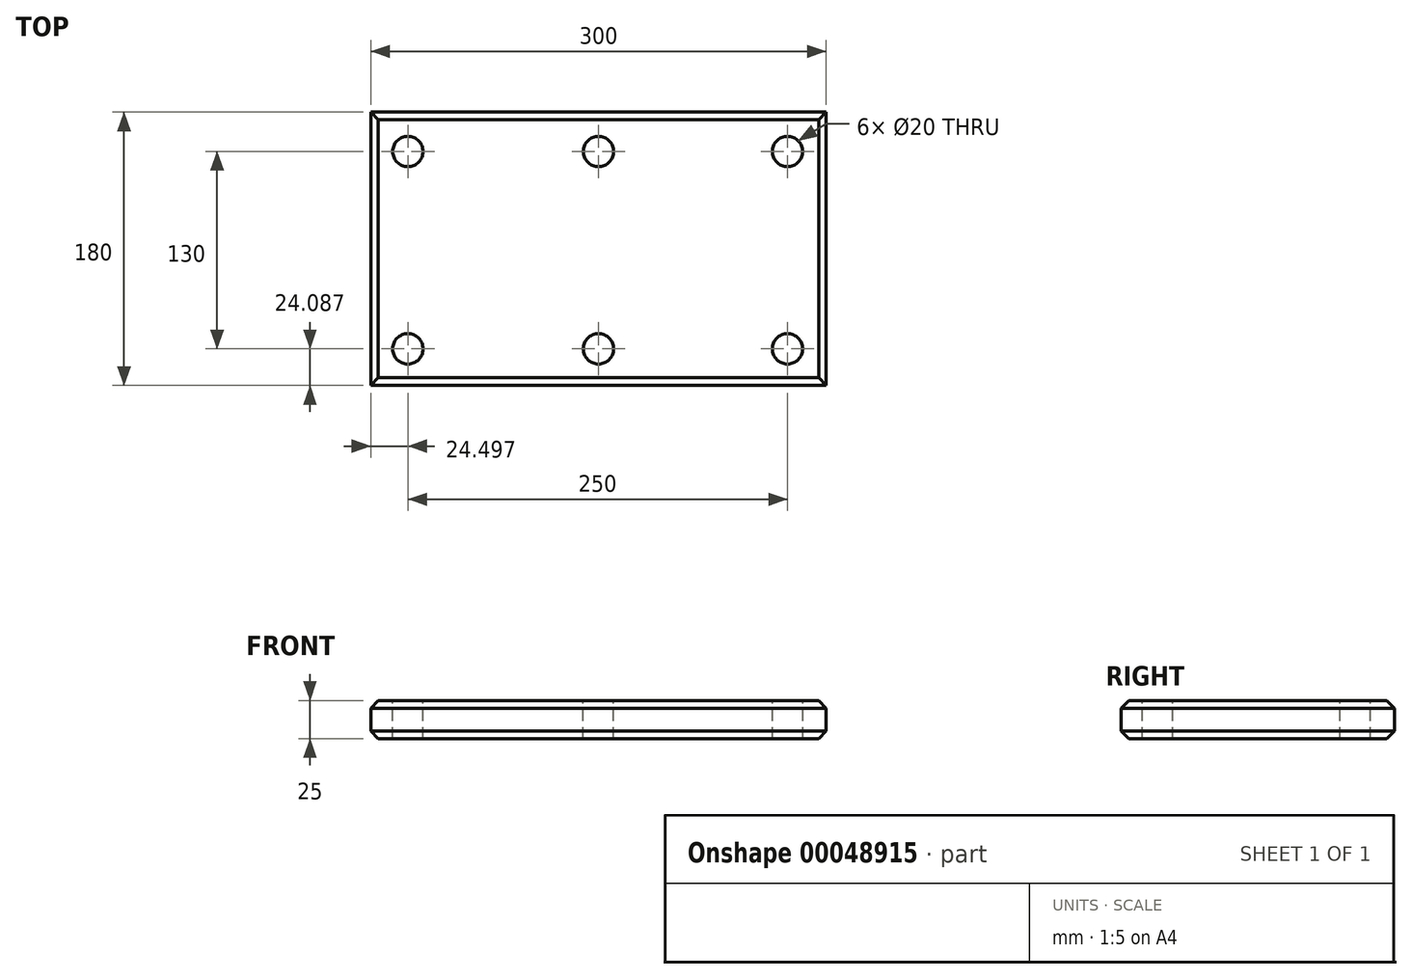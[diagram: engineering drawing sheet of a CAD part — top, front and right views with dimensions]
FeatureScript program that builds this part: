
annotation { "Feature Type Name" : "Feature", "Feature Type Description" : "" }
export const myFeature = defineFeature(function(context is Context, id is Id, definition is map)
    precondition{}
    {
        {
            var Q0;
            Q0=qCreatedBy(makeId("Top.planeOp"),FACE);
            var sketch = newSketch(context, id + "F0", { "sketchPlane" : qUnion([Q0])});
            skLineSegment(sketch, "E0.rect.bottom", {"start": v(150, 90) * mm, "end": v(-150, 90) * mm});
            skLineSegment(sketch, "E0.rect.top", {"start": v(150, -90) * mm, "end": v(-150, -90) * mm});
            skLineSegment(sketch, "E0.rect.left", {"start": v(150, 90) * mm, "end": v(150, -90) * mm});
            skLineSegment(sketch, "E0.rect.right", {"start": v(-150, 90) * mm, "end": v(-150, -90) * mm});
            skPoint(sketch, "E0.rect.middle", {"position": v(0, 0) * mm});
            skSolve(sketch);
        }
        {
            var Q0;
            Q0=makeQuery(id+"F0.imprint","IMPRINT",FACE,{"disambiguationData":[TD([[makeQuery(id+"F0.imprint","IMPRINT",EDGE,{"derivedFrom":sQuery(id+"F0.wireOp",EDGE,"E0.rect.bottom")}),1.0]])]});
            extrude(context, id + "F1", {"entities" : qUnion([Q0]), "depth" : 25 * mm});
        }
        {
            var Q0;
            Q0=makeQuery(id+"F1.opExtrude","CAP_FACE",FACE,{"disambiguationData":[OSD([sQuery(id+"F0.wireOp",EDGE,"E0.rect.bottom"),sQuery(id+"F0.wireOp",EDGE,"E0.rect.top"),sQuery(id+"F0.wireOp",EDGE,"E0.rect.left"),sQuery(id+"F0.wireOp",EDGE,"E0.rect.right")])],"isStart":false});
            var sketch = newSketch(context, id + "F2", { "sketchPlane" : qUnion([Q0])});
            skCircle(sketch, "E1", {"center": v(-125.5, 64.09) * mm, "radius": 10 * mm});
            skLineSegment(sketch, "E2", {"start": v(-125.5, 64.09) * mm, "end": v(124.5, 64.09) * mm, "construction": true});
            skCircle(sketch, "E3", {"center": v(124.5, 64.09) * mm, "radius": 10 * mm});
            skLineSegment(sketch, "E4", {"start": v(-125.5, 64.09) * mm, "end": v(-125.5, -65.91) * mm, "construction": true});
            skCircle(sketch, "E5", {"center": v(-125.5, -65.91) * mm, "radius": 10 * mm});
            skLineSegment(sketch, "E6", {"start": v(-125.5, -65.91) * mm, "end": v(124.5, -65.91) * mm, "construction": true});
            skCircle(sketch, "E7", {"center": v(124.5, -65.91) * mm, "radius": 10 * mm});
            skLineSegment(sketch, "E8", {"start": v(124.5, -65.91) * mm, "end": v(124.5, 64.09) * mm, "construction": true});
            skCircle(sketch, "E9", {"center": v(0, 64.09) * mm, "radius": 10 * mm});
            skCircle(sketch, "E10", {"center": v(0, -65.91) * mm, "radius": 10 * mm});
            skSolve(sketch);
        }
        {
            var Q0;
            Q0=makeQuery(id+"F2.imprint","IMPRINT",FACE,{"disambiguationData":[TD([[makeQuery(id+"F2.imprint","IMPRINT",EDGE,{"derivedFrom":sQuery(id+"F2.wireOp",EDGE,"E9")}),1.0]])]});
            var Q1;
            Q1=makeQuery(id+"F2.imprint","IMPRINT",FACE,{"disambiguationData":[TD([[makeQuery(id+"F2.imprint","IMPRINT",EDGE,{"derivedFrom":sQuery(id+"F2.wireOp",EDGE,"E1")}),1.0]])]});
            var Q2;
            Q2=makeQuery(id+"F2.imprint","IMPRINT",FACE,{"disambiguationData":[TD([[makeQuery(id+"F2.imprint","IMPRINT",EDGE,{"derivedFrom":sQuery(id+"F2.wireOp",EDGE,"E5")}),1.0]])]});
            var Q3;
            Q3=makeQuery(id+"F2.imprint","IMPRINT",FACE,{"disambiguationData":[TD([[makeQuery(id+"F2.imprint","IMPRINT",EDGE,{"derivedFrom":sQuery(id+"F2.wireOp",EDGE,"E10")}),1.0]])]});
            var Q4;
            Q4=makeQuery(id+"F2.imprint","IMPRINT",FACE,{"disambiguationData":[TD([[makeQuery(id+"F2.imprint","IMPRINT",EDGE,{"derivedFrom":sQuery(id+"F2.wireOp",EDGE,"E7")}),1.0]])]});
            var Q5;
            Q5=makeQuery(id+"F2.imprint","IMPRINT",FACE,{"disambiguationData":[TD([[makeQuery(id+"F2.imprint","IMPRINT",EDGE,{"derivedFrom":sQuery(id+"F2.wireOp",EDGE,"E3")}),1.0]])]});
            extrude(context, id + "F3", {"entities" : qUnion([Q0, Q1, Q2, Q3, Q4, Q5]), "operationType" : NewBodyOperationType.REMOVE, "endBound" : BoundingType.THROUGH_ALL, "oppositeDirection" : true, "depth" : 25 * mm});
        }
        {
            var Q0;
            Q0=makeQuery(id+"F1.opExtrude","CAP_EDGE",EDGE,{"disambiguationData":[OSD([sQuery(id+"F0.wireOp",EDGE,"E0.rect.bottom")])],"isStart":false});
            var Q1;
            Q1=makeQuery(id+"F1.opExtrude","CAP_EDGE",EDGE,{"disambiguationData":[OSD([sQuery(id+"F0.wireOp",EDGE,"E0.rect.left")])],"isStart":false});
            var Q2;
            Q2=makeQuery(id+"F1.opExtrude","CAP_EDGE",EDGE,{"disambiguationData":[OSD([sQuery(id+"F0.wireOp",EDGE,"E0.rect.top")])],"isStart":false});
            var Q3;
            Q3=makeQuery(id+"F1.opExtrude","CAP_EDGE",EDGE,{"disambiguationData":[OSD([sQuery(id+"F0.wireOp",EDGE,"E0.rect.right")])],"isStart":false});
            var Q4;
            Q4=makeQuery(id+"F1.opExtrude","CAP_EDGE",EDGE,{"disambiguationData":[OSD([sQuery(id+"F0.wireOp",EDGE,"E0.rect.top")])],"isStart":true});
            var Q5;
            Q5=makeQuery(id+"F1.opExtrude","CAP_EDGE",EDGE,{"disambiguationData":[OSD([sQuery(id+"F0.wireOp",EDGE,"E0.rect.left")])],"isStart":true});
            var Q6;
            Q6=makeQuery(id+"F1.opExtrude","CAP_EDGE",EDGE,{"disambiguationData":[OSD([sQuery(id+"F0.wireOp",EDGE,"E0.rect.bottom")])],"isStart":true});
            var Q7;
            Q7=makeQuery(id+"F1.opExtrude","CAP_EDGE",EDGE,{"disambiguationData":[OSD([sQuery(id+"F0.wireOp",EDGE,"E0.rect.right")])],"isStart":true});
            chamfer(context, id + "F4", {"entities" : qUnion([Q0, Q1, Q2, Q3, Q4, Q5, Q6, Q7]), "width" : 5 * mm, "tangentPropagation" : true});
        }
    });
